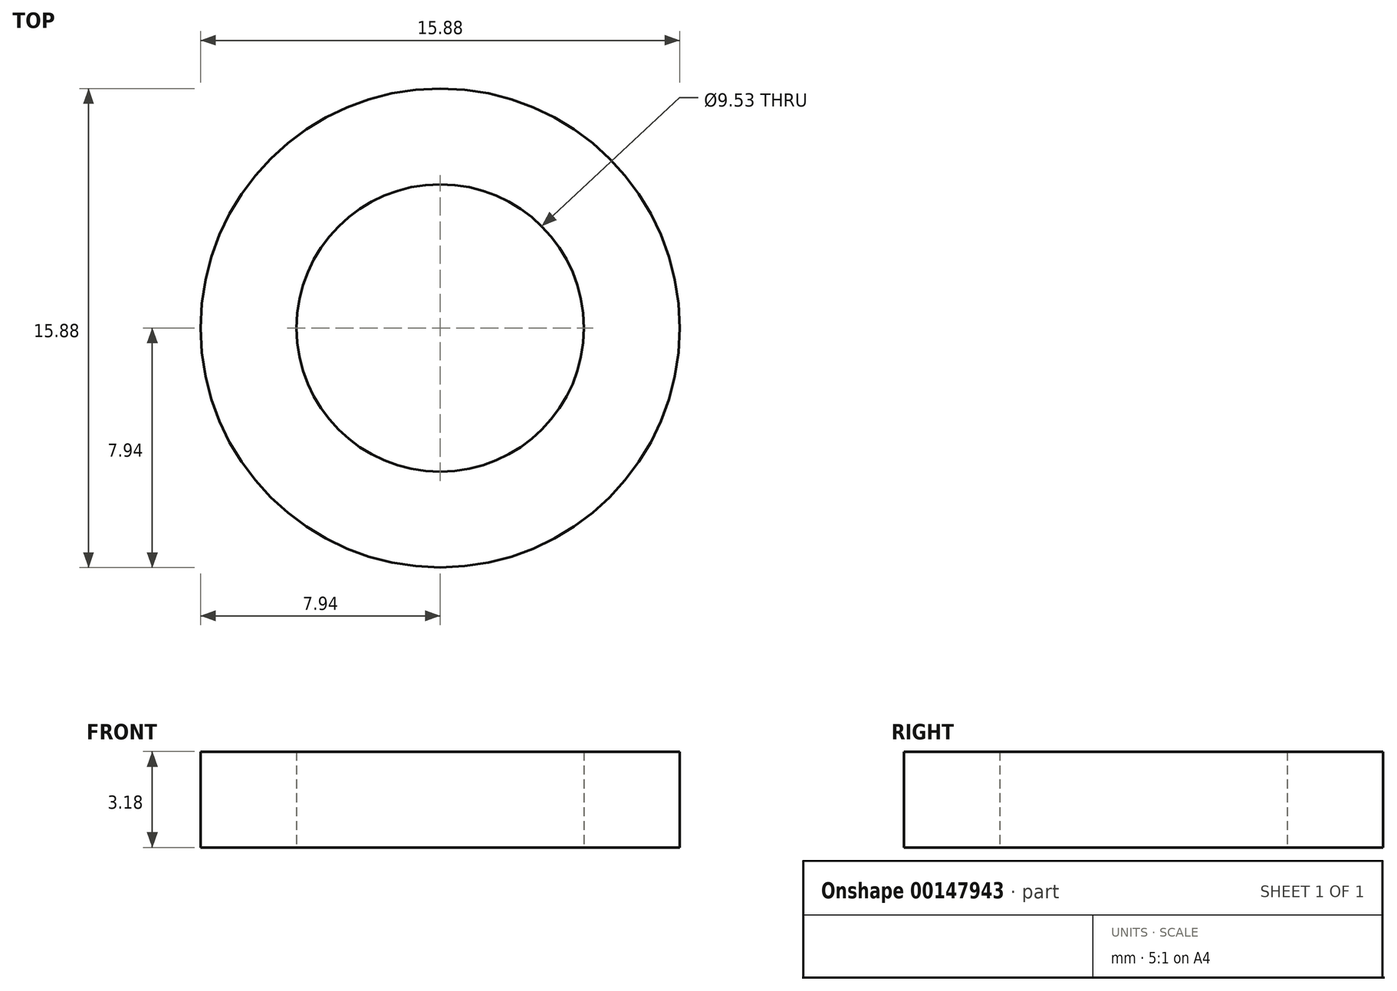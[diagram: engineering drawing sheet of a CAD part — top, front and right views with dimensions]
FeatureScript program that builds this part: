
annotation { "Feature Type Name" : "Feature", "Feature Type Description" : "" }
export const myFeature = defineFeature(function(context is Context, id is Id, definition is map)
    precondition{}
    {
        {
            var Q0;
            Q0=qCreatedBy(makeId("Top.planeOp"),FACE);
            var sketch = newSketch(context, id + "F0", { "sketchPlane" : qUnion([Q0])});
            skCircle(sketch, "E0", {"center": v(0, 0) * mm, "radius": 4.76 * mm});
            skCircle(sketch, "E1", {"center": v(0, 0) * mm, "radius": 7.94 * mm});
            skSolve(sketch);
        }
        {
            var Q0;
            Q0=qSketchRegion(id+"F0",true);
            extrude(context, id + "F1", {"entities" : qUnion([Q0]), "depth" : 3.17 * mm});
        }
    });
